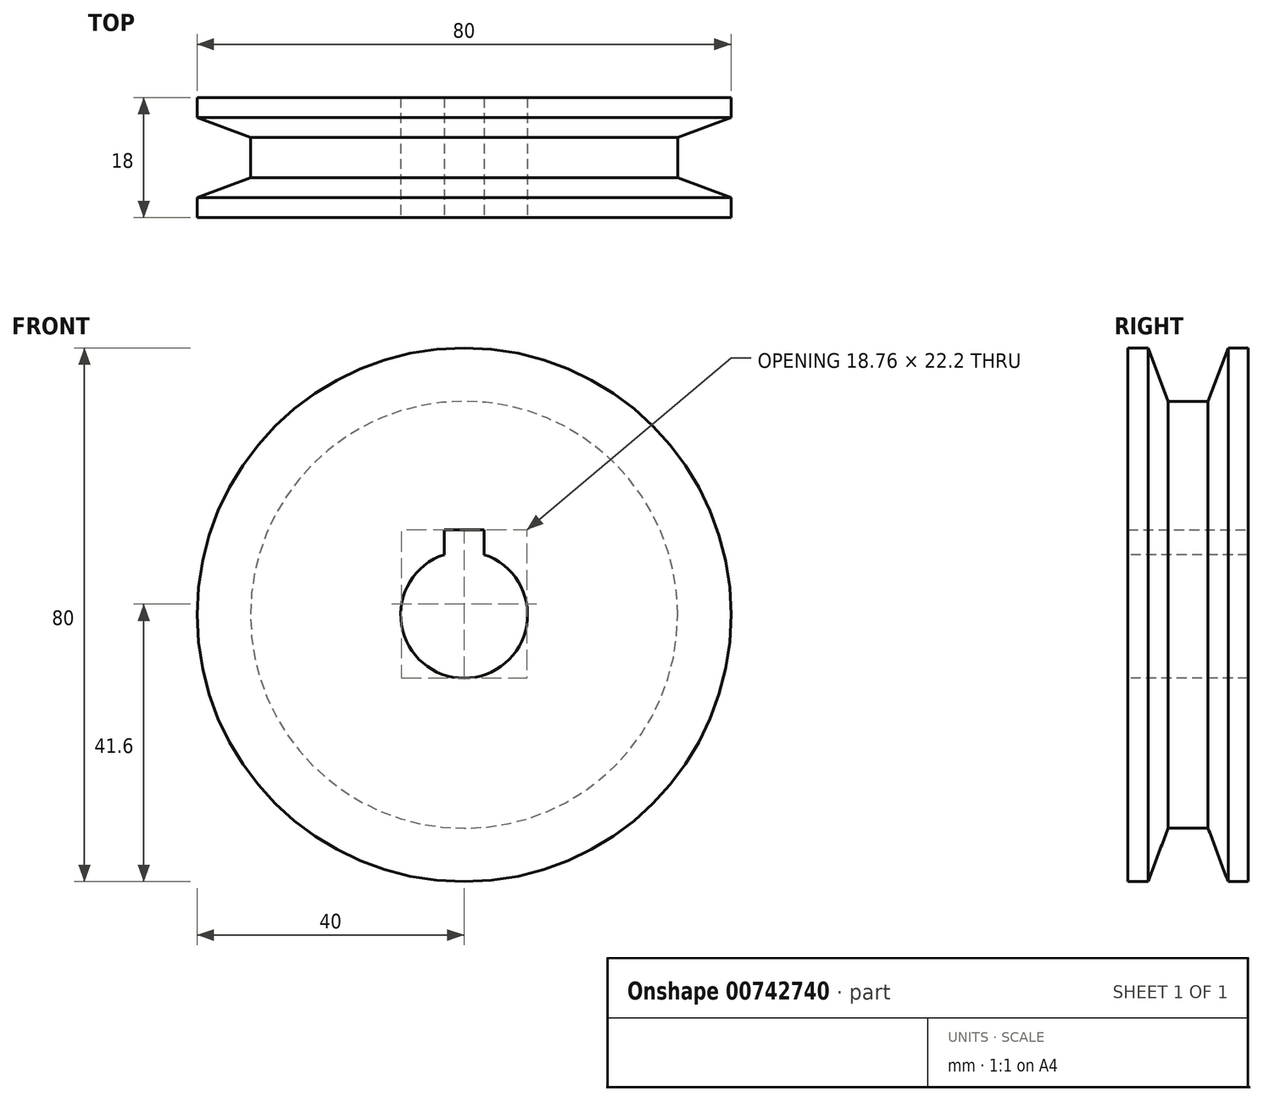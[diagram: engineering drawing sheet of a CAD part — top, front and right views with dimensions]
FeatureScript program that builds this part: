
annotation { "Feature Type Name" : "Feature", "Feature Type Description" : "" }
export const myFeature = defineFeature(function(context is Context, id is Id, definition is map)
    precondition{}
    {
        {
            var Q0;
            Q0=qCreatedBy(makeId("Top.planeOp"),FACE);
            var sketch = newSketch(context, id + "F0", { "sketchPlane" : qUnion([Q0])});
            skLineSegment(sketch, "E0", {"start": v(-9.5, 0) * mm, "end": v(-9.5, 18) * mm});
            skLineSegment(sketch, "E1", {"start": v(-9.5, 0) * mm, "end": v(-40, 0) * mm});
            skLineSegment(sketch, "E2", {"start": v(-40, 0) * mm, "end": v(-40, 3) * mm});
            skLineSegment(sketch, "E3", {"start": v(-40, 3) * mm, "end": v(-32, 6) * mm});
            skLineSegment(sketch, "E4", {"start": v(-32, 6) * mm, "end": v(-32, 12) * mm});
            skLineSegment(sketch, "E5", {"start": v(-32, 12) * mm, "end": v(-40, 15) * mm});
            skLineSegment(sketch, "E6", {"start": v(-40, 15) * mm, "end": v(-40, 18) * mm});
            skLineSegment(sketch, "E7", {"start": v(-40, 18) * mm, "end": v(-9.5, 18) * mm});
            skLineSegment(sketch, "E8", {"start": v(0, -6.86) * mm, "end": v(0, 28.65) * mm});
            skSolve(sketch);
        }
        {
            var Q0;
            Q0=makeQuery(id+"F0.imprint","IMPRINT",FACE,{"disambiguationData":[TD([[makeQuery(id+"F0.imprint","IMPRINT",EDGE,{"derivedFrom":sQuery(id+"F0.wireOp",EDGE,"E0")}),1.0]])]});
            var Q1;
            Q1=sQuery(id+"F0.wireOp",EDGE,"E8");
            revolve(context, id + "F1", {"surfaceOperationType" : NewSurfaceOperationType.NEW, "entities" : qUnion([Q0]), "axis" : qUnion([Q1]), "revolveType" : RevolveType.FULL});
        }
        {
            var Q0;
            Q0=makeQuery(id+"F1.opRevolve","SWEPT_FACE",FACE,{"disambiguationData":[OSD([sQuery(id+"F0.wireOp",EDGE,"E7")])]});
            var sketch = newSketch(context, id + "F2", { "sketchPlane" : qUnion([Q0])});
            skLineSegment(sketch, "E9", {"start": v(-3, 12.7) * mm, "end": v(-3, 3.29) * mm});
            skLineSegment(sketch, "E10", {"start": v(-3, 3.29) * mm, "end": v(3, 3.29) * mm});
            skLineSegment(sketch, "E11", {"start": v(3, 3.29) * mm, "end": v(3, 12.7) * mm});
            skLineSegment(sketch, "E12", {"start": v(3, 12.7) * mm, "end": v(-3, 12.7) * mm});
            skSolve(sketch);
        }
        {
            var Q0;
            Q0 = qSketchRegion(id + "F2", true);
            extrude(context, id + "F3", {"entities" : qUnion([Q0]), "operationType" : NewBodyOperationType.REMOVE, "oppositeDirection" : true, "depth" : 25 * mm, "offsetDistance" : 25 * mm});
        }
    });
